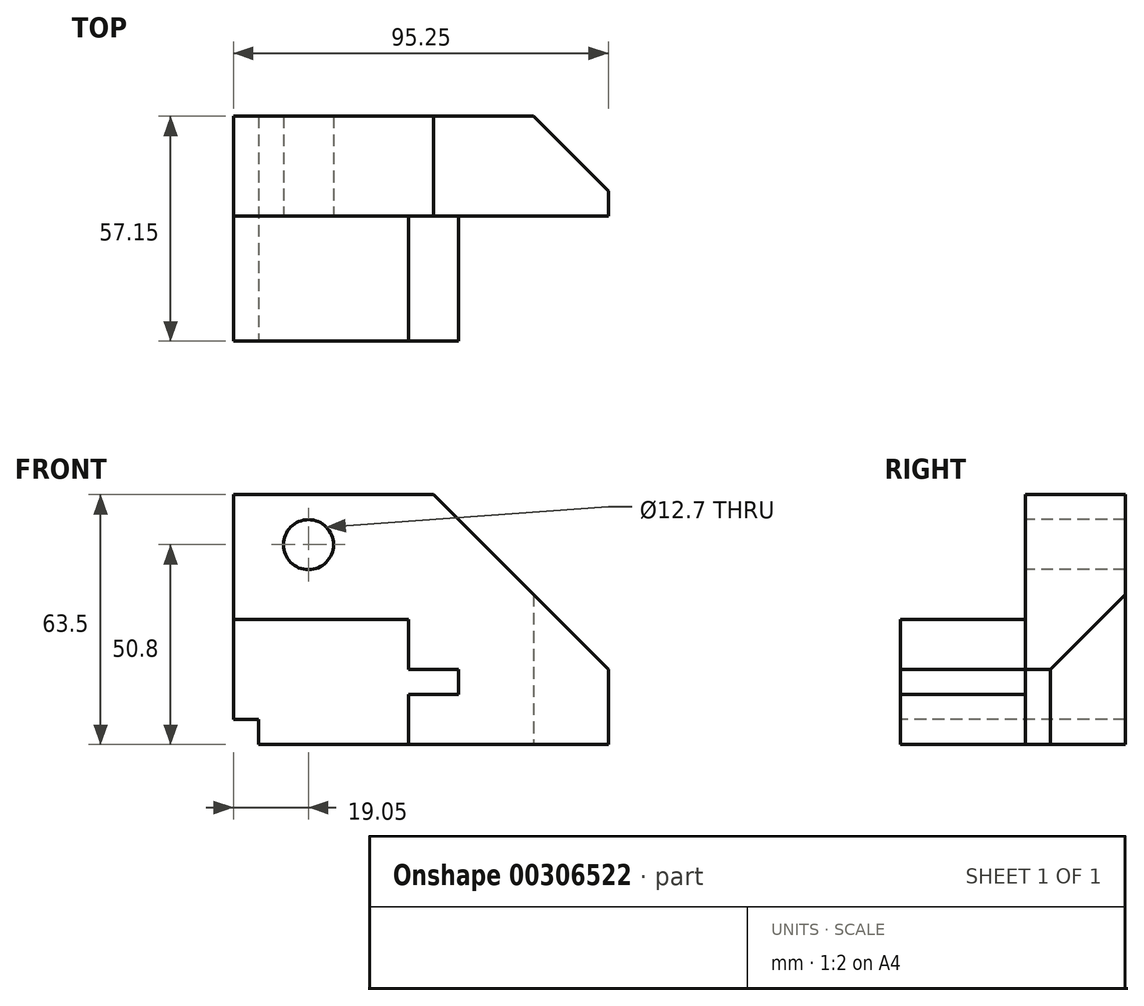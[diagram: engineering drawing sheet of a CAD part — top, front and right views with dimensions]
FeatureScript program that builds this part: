
annotation { "Feature Type Name" : "Feature", "Feature Type Description" : "" }
export const myFeature = defineFeature(function(context is Context, id is Id, definition is map)
    precondition{}
    {
        {
            var Q0;
            Q0=qCreatedBy(makeId("Front.planeOp"),FACE);
            var sketch = newSketch(context, id + "F0", { "sketchPlane" : qUnion([Q0])});
            skLineSegment(sketch, "E0.bottom", {"start": v(0, 0) * mm, "end": v(107.95, 0) * mm});
            skLineSegment(sketch, "E0.top", {"start": v(0, 63.5) * mm, "end": v(107.95, 63.5) * mm});
            skLineSegment(sketch, "E0.left", {"start": v(0, 0) * mm, "end": v(0, 63.5) * mm});
            skLineSegment(sketch, "E0.right", {"start": v(107.95, 0) * mm, "end": v(107.95, 63.5) * mm});
            skSolve(sketch);
        }
        {
            var Q0;
            Q0=makeQuery(id+"F0.imprint","IMPRINT",FACE,{"disambiguationData":[TD([[makeQuery(id+"F0.imprint","IMPRINT",EDGE,{"derivedFrom":sQuery(id+"F0.wireOp",EDGE,"E0.bottom")}),1.0]])]});
            extrude(context, id + "F1", {"entities" : qUnion([Q0]), "oppositeDirection" : true, "depth" : 57.15 * mm});
        }
        {
            var Q0;
            Q0=makeQuery(id+"F1.opExtrude","SWEPT_FACE",FACE,{"disambiguationData":[OSD([sQuery(id+"F0.wireOp",EDGE,"E0.top")])]});
            var sketch = newSketch(context, id + "F2", { "sketchPlane" : qUnion([Q0])});
            skLineSegment(sketch, "E1.bottom", {"start": v(0, 0) * mm, "end": v(44.45, 0) * mm});
            skLineSegment(sketch, "E1.top", {"start": v(0, 31.75) * mm, "end": v(44.45, 31.75) * mm});
            skLineSegment(sketch, "E1.left", {"start": v(0, 0) * mm, "end": v(0, 31.75) * mm});
            skLineSegment(sketch, "E1.right", {"start": v(44.45, 0) * mm, "end": v(44.45, 31.75) * mm});
            skSolve(sketch);
        }
        {
            var Q0;
            Q0 = qSketchRegion(id + "F2", true);
            extrude(context, id + "F3", {"entities" : qUnion([Q0]), "operationType" : NewBodyOperationType.REMOVE, "oppositeDirection" : true, "depth" : 31.75 * mm});
        }
        {
            var Q0;
            Q0=makeQuery(id+"F1.opExtrude","SWEPT_FACE",FACE,{"disambiguationData":[OSD([sQuery(id+"F0.wireOp",EDGE,"E0.top")])]});
            var sketch = newSketch(context, id + "F4", { "sketchPlane" : qUnion([Q0])});
            skLineSegment(sketch, "E2.bottom", {"start": v(44.45, 31.75) * mm, "end": v(107.95, 31.75) * mm});
            skLineSegment(sketch, "E2.top", {"start": v(44.45, 0) * mm, "end": v(107.95, 0) * mm});
            skLineSegment(sketch, "E2.left", {"start": v(44.45, 31.75) * mm, "end": v(44.45, 0) * mm});
            skLineSegment(sketch, "E2.right", {"start": v(107.95, 31.75) * mm, "end": v(107.95, 0) * mm});
            skSolve(sketch);
        }
        {
            var Q0;
            Q0 = qSketchRegion(id + "F4", true);
            extrude(context, id + "F5", {"entities" : qUnion([Q0]), "operationType" : NewBodyOperationType.REMOVE, "oppositeDirection" : true, "depth" : 44.45 * mm});
        }
        {
            var Q0;
            Q0=qCreatedBy(makeId("Front.planeOp"),FACE);
            var sketch = newSketch(context, id + "F6", { "sketchPlane" : qUnion([Q0])});
            skLineSegment(sketch, "E3.bottom", {"start": v(0, 0) * mm, "end": v(6.35, 0) * mm});
            skLineSegment(sketch, "E3.top", {"start": v(0, 6.35) * mm, "end": v(6.35, 6.35) * mm});
            skLineSegment(sketch, "E3.left", {"start": v(0, 0) * mm, "end": v(0, 6.35) * mm});
            skLineSegment(sketch, "E3.right", {"start": v(6.35, 0) * mm, "end": v(6.35, 6.35) * mm});
            skSolve(sketch);
        }
        {
            var Q0;
            Q0 = qSketchRegion(id + "F6", true);
            extrude(context, id + "F7", {"entities" : qUnion([Q0]), "operationType" : NewBodyOperationType.REMOVE, "endBound" : BoundingType.THROUGH_ALL, "oppositeDirection" : true, "depth" : 25.4 * mm});
        }
        {
            var Q0;
            Q0=makeQuery(id+"F1.opExtrude","CAP_FACE",FACE,{"disambiguationData":[OSD([sQuery(id+"F0.wireOp",EDGE,"E0.bottom"),sQuery(id+"F0.wireOp",EDGE,"E0.top"),sQuery(id+"F0.wireOp",EDGE,"E0.left"),sQuery(id+"F0.wireOp",EDGE,"E0.right")])],"isStart":true});
            var sketch = newSketch(context, id + "F8", { "sketchPlane" : qUnion([Q0])});
            skLineSegment(sketch, "E4", {"start": v(44.45, 0) * mm, "end": v(44.45, 12.7) * mm});
            skLineSegment(sketch, "E5", {"start": v(44.45, 12.7) * mm, "end": v(57.15, 12.7) * mm});
            skLineSegment(sketch, "E6", {"start": v(57.15, 12.7) * mm, "end": v(57.15, 19.05) * mm});
            skLineSegment(sketch, "E7", {"start": v(57.15, 19.05) * mm, "end": v(107.95, 19.05) * mm});
            skLineSegment(sketch, "E8", {"start": v(107.95, 19.05) * mm, "end": v(107.95, 0) * mm});
            skLineSegment(sketch, "E9", {"start": v(107.95, 0) * mm, "end": v(44.45, 0) * mm});
            skSolve(sketch);
        }
        {
            var Q0;
            Q0 = qSketchRegion(id + "F8", true);
            extrude(context, id + "F9", {"entities" : qUnion([Q0]), "operationType" : NewBodyOperationType.REMOVE, "oppositeDirection" : true, "depth" : 31.75 * mm});
        }
        {
            var Q0;
            Q0=makeQuery(id+"F9.boolean.opBoolean","MERGE",FACE,{"derivedFrom":[makeQuery(id+"F5.boolean.opBoolean","MERGE",FACE,{"derivedFrom":[makeQuery(id+"F3.boolean.opBoolean","COPY",FACE,{"derivedFrom":makeQuery(id+"F3.opExtrude","SWEPT_FACE",FACE,{"disambiguationData":[OSD([sQuery(id+"F2.wireOp",EDGE,"E1.top")])]})}),makeQuery(id+"F5.opExtrude","SWEPT_FACE",FACE,{"disambiguationData":[OSD([sQuery(id+"F4.wireOp",EDGE,"E2.bottom")])]})]}),makeQuery(id+"F9.opExtrude","CAP_FACE",FACE,{"disambiguationData":[OSD([sQuery(id+"F8.wireOp",EDGE,"E4"),sQuery(id+"F8.wireOp",EDGE,"E5"),sQuery(id+"F8.wireOp",EDGE,"E6"),sQuery(id+"F8.wireOp",EDGE,"E7"),sQuery(id+"F8.wireOp",EDGE,"E8"),sQuery(id+"F8.wireOp",EDGE,"E9")])],"isStart":false})]});
            var sketch = newSketch(context, id + "F10", { "sketchPlane" : qUnion([Q0])});
            skLineSegment(sketch, "E10.bottom", {"start": v(107.95, 0) * mm, "end": v(95.25, 0) * mm});
            skLineSegment(sketch, "E10.top", {"start": v(107.95, 63.5) * mm, "end": v(95.25, 63.5) * mm});
            skLineSegment(sketch, "E10.left", {"start": v(107.95, 0) * mm, "end": v(107.95, 63.5) * mm});
            skLineSegment(sketch, "E10.right", {"start": v(95.25, 0) * mm, "end": v(95.25, 63.5) * mm});
            skSolve(sketch);
        }
        {
            var Q0;
            Q0 = qSketchRegion(id + "F10", true);
            extrude(context, id + "F11", {"entities" : qUnion([Q0]), "operationType" : NewBodyOperationType.REMOVE, "oppositeDirection" : true, "depth" : 25.4 * mm});
        }
        {
            var Q0;
            Q0=makeQuery(id+"F9.boolean.opBoolean","MERGE",FACE,{"derivedFrom":[makeQuery(id+"F5.boolean.opBoolean","MERGE",FACE,{"derivedFrom":[makeQuery(id+"F3.boolean.opBoolean","COPY",FACE,{"derivedFrom":makeQuery(id+"F3.opExtrude","SWEPT_FACE",FACE,{"disambiguationData":[OSD([sQuery(id+"F2.wireOp",EDGE,"E1.top")])]})}),makeQuery(id+"F5.opExtrude","SWEPT_FACE",FACE,{"disambiguationData":[OSD([sQuery(id+"F4.wireOp",EDGE,"E2.bottom")])]})]}),makeQuery(id+"F9.opExtrude","CAP_FACE",FACE,{"disambiguationData":[OSD([sQuery(id+"F8.wireOp",EDGE,"E4"),sQuery(id+"F8.wireOp",EDGE,"E5"),sQuery(id+"F8.wireOp",EDGE,"E6"),sQuery(id+"F8.wireOp",EDGE,"E7"),sQuery(id+"F8.wireOp",EDGE,"E8"),sQuery(id+"F8.wireOp",EDGE,"E9")])],"isStart":false})]});
            var sketch = newSketch(context, id + "F12", { "sketchPlane" : qUnion([Q0])});
            skLineSegment(sketch, "E11", {"start": v(50.8, 63.5) * mm, "end": v(95.25, 19.05) * mm});
            skLineSegment(sketch, "E12", {"start": v(95.25, 19.05) * mm, "end": v(95.25, 63.5) * mm});
            skLineSegment(sketch, "E13", {"start": v(95.25, 63.5) * mm, "end": v(50.8, 63.5) * mm});
            skSolve(sketch);
        }
        {
            var Q0;
            Q0 = qSketchRegion(id + "F12", true);
            extrude(context, id + "F13", {"entities" : qUnion([Q0]), "operationType" : NewBodyOperationType.REMOVE, "endBound" : BoundingType.THROUGH_ALL, "oppositeDirection" : true, "depth" : 25.4 * mm});
        }
        {
            var Q0;
            Q0=makeQuery(id+"F9.boolean.opBoolean","MERGE",FACE,{"derivedFrom":[makeQuery(id+"F5.boolean.opBoolean","MERGE",FACE,{"derivedFrom":[makeQuery(id+"F3.boolean.opBoolean","COPY",FACE,{"derivedFrom":makeQuery(id+"F3.opExtrude","SWEPT_FACE",FACE,{"disambiguationData":[OSD([sQuery(id+"F2.wireOp",EDGE,"E1.top")])]})}),makeQuery(id+"F5.opExtrude","SWEPT_FACE",FACE,{"disambiguationData":[OSD([sQuery(id+"F4.wireOp",EDGE,"E2.bottom")])]})]}),makeQuery(id+"F9.opExtrude","CAP_FACE",FACE,{"disambiguationData":[OSD([sQuery(id+"F8.wireOp",EDGE,"E4"),sQuery(id+"F8.wireOp",EDGE,"E5"),sQuery(id+"F8.wireOp",EDGE,"E6"),sQuery(id+"F8.wireOp",EDGE,"E7"),sQuery(id+"F8.wireOp",EDGE,"E8"),sQuery(id+"F8.wireOp",EDGE,"E9")])],"isStart":false})]});
            var sketch = newSketch(context, id + "F14", { "sketchPlane" : qUnion([Q0])});
            skCircle(sketch, "E14", {"center": v(19.05, 50.8) * mm, "radius": 6.35 * mm});
            skSolve(sketch);
        }
        {
            var Q0;
            Q0 = qSketchRegion(id + "F14", true);
            extrude(context, id + "F15", {"entities" : qUnion([Q0]), "operationType" : NewBodyOperationType.REMOVE, "endBound" : BoundingType.THROUGH_ALL, "oppositeDirection" : true, "depth" : 25.4 * mm});
        }
        {
            var Q0;
            Q0=qCreatedBy(makeId("Top.planeOp"),FACE);
            var sketch = newSketch(context, id + "F16", { "sketchPlane" : qUnion([Q0])});
            skLineSegment(sketch, "E15", {"start": v(95.25, 57.15) * mm, "end": v(76.2, 57.15) * mm});
            skLineSegment(sketch, "E16", {"start": v(76.2, 57.15) * mm, "end": v(95.25, 38.1) * mm});
            skLineSegment(sketch, "E17", {"start": v(95.25, 38.1) * mm, "end": v(95.25, 57.15) * mm});
            skSolve(sketch);
        }
        {
            var Q0;
            Q0 = qSketchRegion(id + "F16", true);
            extrude(context, id + "F17", {"entities" : qUnion([Q0]), "operationType" : NewBodyOperationType.REMOVE, "endBound" : BoundingType.THROUGH_ALL, "depth" : 25.4 * mm});
        }
    });
